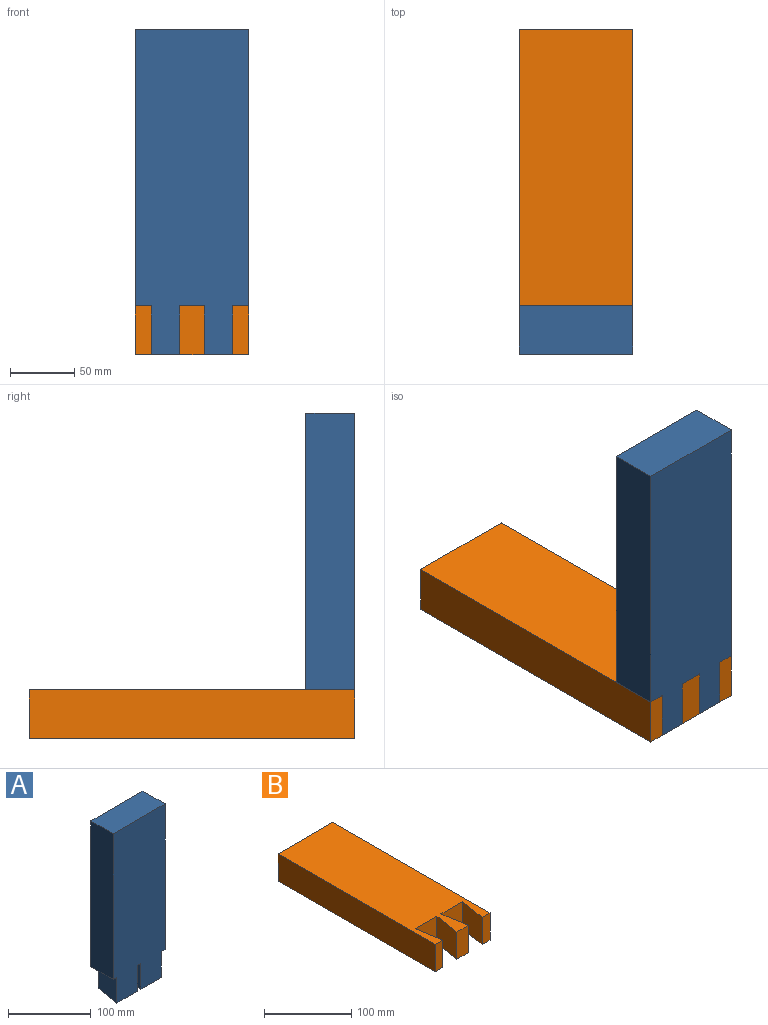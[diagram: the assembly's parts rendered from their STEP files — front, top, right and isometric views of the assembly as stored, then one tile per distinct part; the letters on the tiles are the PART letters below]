
ASSEMBLY  parts=2 mates=1
PART A: 14 faces, bbox 88.9x38.1x254 mm
  f0: plane 215.9x38.1mm, normal (-1,0,0), area 8225.8mm2, adj f4,f5,f6,f13
  f1: plane 38.1x34.93mm, normal (0,0,-1), area 1088.7mm2, adj f4,f5,f7,f12
  f2: plane 38.1x34.93mm, normal (0,0,-1), area 1088.7mm2, adj f4,f5,f8,f10
  f3: plane 215.9x38.1mm, normal (1,0,0), area 8225.8mm2, adj f4,f5,f6,f11
  f4: plane 254x88.9mm, normal (0,-1,0), area 21854.8mm2, adj f0,f1,f2,f3,f6,f7,f8,f9
  f5: plane 254x88.9mm, normal (0,1,0), area 20887.1mm2, adj f0,f1,f2,f3,f6,f7,f8,f9
  f6: plane 88.9x38.1mm, normal (0,0,1), area 3387.1mm2, adj f0,f3,f4,f5
  f7: plane 38.1x38.1mm, normal (0.99,0.16,0), area 1471.6mm2, adj f1,f4,f5,f9
  f8: plane 38.1x38.1mm, normal (-0.99,0.16,0), area 1471.6mm2, adj f2,f4,f5,f9
  f9: plane 38.1x19.05mm, normal (0,0,-1), area 483.9mm2, adj f4,f5,f7,f8
  f10: plane 38.1x38.1mm, normal (0.99,0.16,0), area 1471.6mm2, adj f2,f4,f5,f11
  f11: plane 38.1x12.7mm, normal (0,0,-1), area 362.9mm2, adj f3,f4,f5,f10
  f12: plane 38.1x38.1mm, normal (-0.99,0.16,0), area 1471.6mm2, adj f1,f4,f5,f13
  f13: plane 38.1x12.7mm, normal (0,0,-1), area 362.9mm2, adj f0,f4,f5,f12
PART B: 14 faces, bbox 88.9x254x38.1 mm
  f0: plane 38.1x19.05mm, normal (0,-1,0), area 725.8mm2, adj f2,f7,f9,f13
  f1: plane 38.1x12.7mm, normal (0,-1,0), area 483.9mm2, adj f2,f6,f7,f10
  f2: plane 254x88.9mm, normal (0,0,-1), area 20403.2mm2, adj f0,f1,f3,f4,f5,f6,f8,f9
  f3: plane 88.9x38.1mm, normal (0,1,0), area 3387.1mm2, adj f2,f4,f6,f7
  f4: plane 254x38.1mm, normal (-1,0,0), area 9677.4mm2, adj f2,f3,f5,f7
  f5: plane 38.1x12.7mm, normal (0,-1,0), area 483.9mm2, adj f2,f4,f7,f12
  f6: plane 254x38.1mm, normal (1,0,0), area 9677.4mm2, adj f1,f2,f3,f7
  f7: plane 254x88.9mm, normal (0,0,1), area 20403.2mm2, adj f0,f1,f3,f4,f5,f6,f8,f9
  f8: plane 38.1x34.93mm, normal (0,-1,0), area 1330.6mm2, adj f2,f7,f9,f10
  f9: plane 38.1x38.1mm, normal (0.99,0.16,0), area 1471.6mm2, adj f0,f2,f7,f8
  f10: plane 38.1x38.1mm, normal (-0.99,0.16,0), area 1471.6mm2, adj f1,f2,f7,f8
  f11: plane 38.1x34.93mm, normal (0,-1,0), area 1330.6mm2, adj f2,f7,f12,f13
  f12: plane 38.1x38.1mm, normal (0.99,0.16,0), area 1471.6mm2, adj f2,f5,f7,f11
  f13: plane 38.1x38.1mm, normal (-0.99,0.16,0), area 1471.6mm2, adj f0,f2,f7,f11
PLACE A rot(axis=(0,0,1),180deg) t=(-189.51,141.02,509.27)mm
PLACE B t=(-110.08,276.21,378.81)mm
MATE fastened A.f4 <-> B.f11  axis (0,1,0) through (-150.48,179.12,378.81)mm
